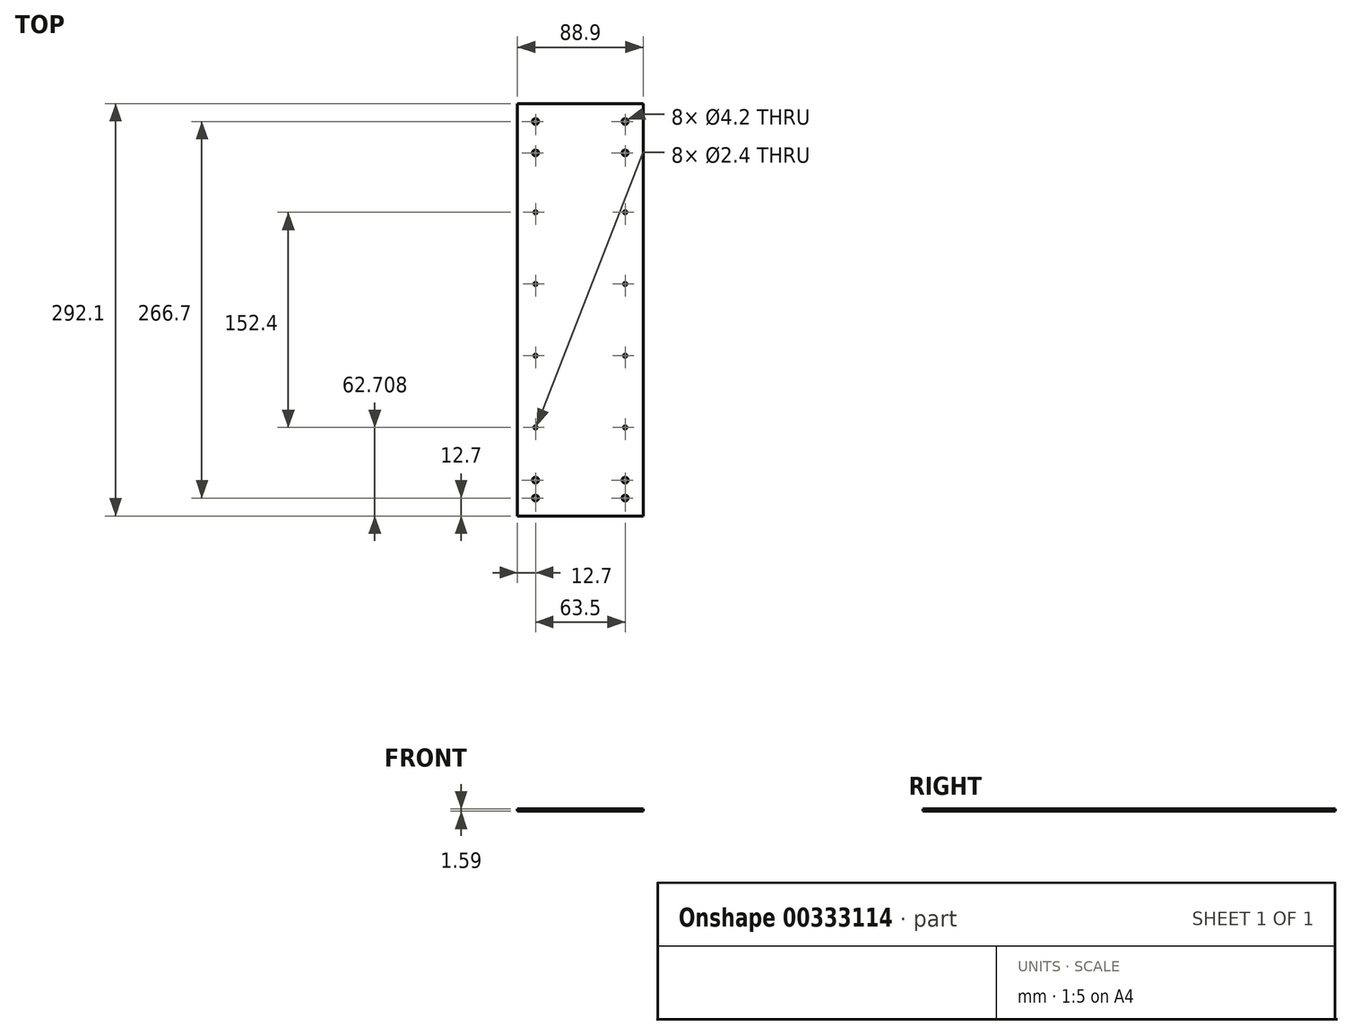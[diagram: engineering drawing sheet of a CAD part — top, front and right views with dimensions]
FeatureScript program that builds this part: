
annotation { "Feature Type Name" : "Feature", "Feature Type Description" : "" }
export const myFeature = defineFeature(function(context is Context, id is Id, definition is map)
    precondition{}
    {
        {
            var Q0;
            Q0=qCreatedBy(makeId("Top.planeOp"),FACE);
            var sketch = newSketch(context, id + "F0", { "sketchPlane" : qUnion([Q0])});
            skLineSegment(sketch, "E0.bottom", {"start": v(-44.45, 146.05) * mm, "end": v(44.45, 146.05) * mm});
            skLineSegment(sketch, "E0.top", {"start": v(-44.45, -146.05) * mm, "end": v(44.45, -146.05) * mm});
            skLineSegment(sketch, "E0.left", {"start": v(-44.45, 146.05) * mm, "end": v(-44.45, -146.05) * mm});
            skLineSegment(sketch, "E0.right", {"start": v(44.45, 146.05) * mm, "end": v(44.45, -146.05) * mm});
            skPoint(sketch, "E0.middle", {"position": v(0, 0) * mm});
            skSolve(sketch);
        }
        {
            var Q0;
            Q0=qSketchRegion(id+"F0",true);
            extrude(context, id + "F1", {"entities" : qUnion([Q0]), "depth" : 1.59 * mm});
        }
        {
            var Q0;
            Q0=makeQuery(id+"F1.opExtrude","CAP_FACE",FACE,{"disambiguationData":[OSD([sQuery(id+"F0.wireOp",EDGE,"E0.bottom"),sQuery(id+"F0.wireOp",EDGE,"E0.top"),sQuery(id+"F0.wireOp",EDGE,"E0.left"),sQuery(id+"F0.wireOp",EDGE,"E0.right")])],"isStart":false});
            var sketch = newSketch(context, id + "F2", { "sketchPlane" : qUnion([Q0])});
            skLineSegment(sketch, "E1", {"start": v(0, 146.05) * mm, "end": v(0, 133.35) * mm, "construction": true});
            skPoint(sketch, "E2", {"position": v(-31.75, 133.35) * mm});
            skPoint(sketch, "E3", {"position": v(31.75, 133.35) * mm});
            skPoint(sketch, "E4", {"position": v(-31.75, 111.13) * mm});
            skPoint(sketch, "E5", {"position": v(31.75, 111.12) * mm});
            skPoint(sketch, "E6", {"position": v(-31.75, -120.65) * mm});
            skPoint(sketch, "E7", {"position": v(31.75, -120.65) * mm});
            skPoint(sketch, "E8", {"position": v(-31.75, -133.35) * mm});
            skPoint(sketch, "E9", {"position": v(31.75, -133.35) * mm});
            skSolve(sketch);
        }
        {
            var Q0;
            Q0=sQuery(id+"F2.wireOp",VERTEX,"E2");
            var Q1;
            Q1=sQuery(id+"F2.wireOp",VERTEX,"E4");
            var Q2;
            Q2=sQuery(id+"F2.wireOp",VERTEX,"E5");
            var Q3;
            Q3=sQuery(id+"F2.wireOp",VERTEX,"E3");
            var Q4;
            Q4=sQuery(id+"F2.wireOp",VERTEX,"E6");
            var Q5;
            Q5=sQuery(id+"F2.wireOp",VERTEX,"E8");
            var Q6;
            Q6=sQuery(id+"F2.wireOp",VERTEX,"E9");
            var Q7;
            Q7=sQuery(id+"F2.wireOp",VERTEX,"E7");
            var Q8;
            Q8=makeQuery(id+"F1.opExtrude","SWEPT_BODY",BODY,{"disambiguationData":[OSD([sQuery(id+"F0.wireOp",EDGE,"E0.bottom"),sQuery(id+"F0.wireOp",EDGE,"E0.top"),sQuery(id+"F0.wireOp",EDGE,"E0.left"),sQuery(id+"F0.wireOp",EDGE,"E0.right")])]});
            hole(context, id + "F3", {"style" : HoleStyle.SIMPLE, "endStyle" : HoleEndStyle.BLIND, "standardTappedOrClearance" : lookupTablePath({ "standard" : "ISO", "engagement" : "75%", "pitch" : "0.8 mm", "size" : "M5", "type" : "Tapped" }), "standardBlindInLast" : lookupTablePath({ "standard" : "ISO", "engagement" : "75%", "pitch" : "0.8 mm", "size" : "M5", "type" : "Tapped" }), "holeDiameter" : 4.2 * mm, "showTappedDepth" : true, "holeDepth" : 15.1 * mm, "tappedDepth" : 12.7 * mm, "tapClearance" : 3, "locations" : qUnion([Q0, Q1, Q2, Q3, Q4, Q5, Q6, Q7]), "scope" : qUnion([Q8]), "majorDiameter" : 5 * mm});
        }
        {
            var Q0;
            Q0=makeQuery(id+"F1.opExtrude","CAP_FACE",FACE,{"disambiguationData":[OSD([sQuery(id+"F0.wireOp",EDGE,"E0.bottom"),sQuery(id+"F0.wireOp",EDGE,"E0.top"),sQuery(id+"F0.wireOp",EDGE,"E0.left"),sQuery(id+"F0.wireOp",EDGE,"E0.right")])],"isStart":false});
            var sketch = newSketch(context, id + "F4", { "sketchPlane" : qUnion([Q0])});
            skLineSegment(sketch, "E10", {"start": v(0, 146.05) * mm, "end": v(0, 100.01) * mm, "construction": true});
            skPoint(sketch, "E11", {"position": v(-31.75, 69.06) * mm});
            skPoint(sketch, "E12", {"position": v(-31.75, 18.26) * mm});
            skPoint(sketch, "E13", {"position": v(-31.75, -32.54) * mm});
            skPoint(sketch, "E14", {"position": v(-31.75, -83.34) * mm});
            skPoint(sketch, "E15.MirrorP", {"position": v(31.75, 69.06) * mm});
            skPoint(sketch, "E16.MirrorP", {"position": v(31.75, 18.26) * mm});
            skPoint(sketch, "E17.MirrorP", {"position": v(31.75, -32.54) * mm});
            skPoint(sketch, "E18.MirrorP", {"position": v(31.75, -83.34) * mm});
            skSolve(sketch);
        }
        {
            var Q0;
            Q0=sQuery(id+"F4.wireOp",VERTEX,"E11");
            var Q1;
            Q1=sQuery(id+"F4.wireOp",VERTEX,"E15.MirrorP");
            var Q2;
            Q2=sQuery(id+"F4.wireOp",VERTEX,"E16.MirrorP");
            var Q3;
            Q3=sQuery(id+"F4.wireOp",VERTEX,"E12");
            var Q4;
            Q4=sQuery(id+"F4.wireOp",VERTEX,"E13");
            var Q5;
            Q5=sQuery(id+"F4.wireOp",VERTEX,"E17.MirrorP");
            var Q6;
            Q6=sQuery(id+"F4.wireOp",VERTEX,"E18.MirrorP");
            var Q7;
            Q7=sQuery(id+"F4.wireOp",VERTEX,"E14");
            var Q8;
            Q8=makeQuery(id+"F1.opExtrude","SWEPT_BODY",BODY,{"disambiguationData":[OSD([sQuery(id+"F0.wireOp",EDGE,"E0.bottom"),sQuery(id+"F0.wireOp",EDGE,"E0.top"),sQuery(id+"F0.wireOp",EDGE,"E0.left"),sQuery(id+"F0.wireOp",EDGE,"E0.right")])]});
            hole(context, id + "F5", {"style" : HoleStyle.SIMPLE, "endStyle" : HoleEndStyle.BLIND, "standardTappedOrClearance" : lookupTablePath({ "standard" : "ISO", "engagement" : "75%", "pitch" : "0.6 mm", "size" : "M3", "type" : "Tapped" }), "standardBlindInLast" : lookupTablePath({ "standard" : "ISO", "engagement" : "75%", "pitch" : "0.6 mm", "size" : "M3", "type" : "Tapped" }), "holeDiameter" : 2.4 * mm, "showTappedDepth" : true, "holeDepth" : 14.48 * mm, "tappedDepth" : 12.68 * mm, "tapClearance" : 3, "locations" : qUnion([Q0, Q1, Q2, Q3, Q4, Q5, Q6, Q7]), "scope" : qUnion([Q8])});
        }
    });
